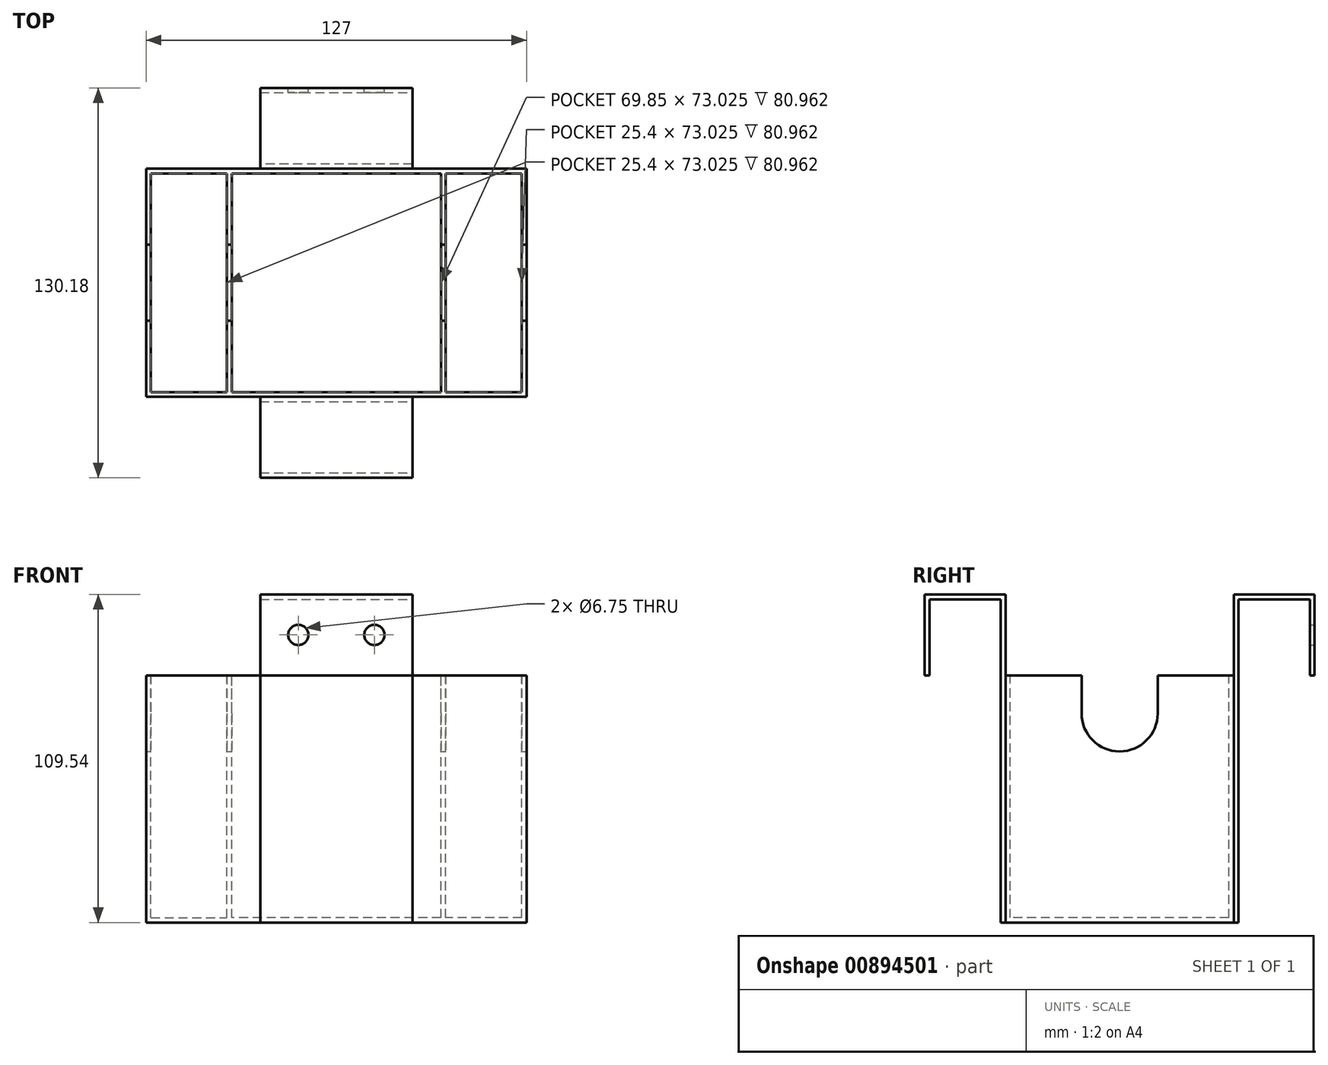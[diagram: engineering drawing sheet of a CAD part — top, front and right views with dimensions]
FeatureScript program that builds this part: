
annotation { "Feature Type Name" : "Feature", "Feature Type Description" : "" }
export const myFeature = defineFeature(function(context is Context, id is Id, definition is map)
    precondition{}
    {
        {
            var Q0;
            Q0=qCreatedBy(makeId("Top.planeOp"),FACE);
            var sketch = newSketch(context, id + "F0", { "sketchPlane" : qUnion([Q0])});
            skLineSegment(sketch, "E0.bottom", {"start": v(63.5, 38.1) * mm, "end": v(-63.5, 38.1) * mm});
            skLineSegment(sketch, "E0.top", {"start": v(63.5, -38.1) * mm, "end": v(-63.5, -38.1) * mm});
            skLineSegment(sketch, "E0.left", {"start": v(63.5, 38.1) * mm, "end": v(63.5, -38.1) * mm});
            skLineSegment(sketch, "E0.right", {"start": v(-63.5, 38.1) * mm, "end": v(-63.5, -38.1) * mm});
            skPoint(sketch, "E1.end.orphan", {"position": v(0, 38.1) * mm});
            skPoint(sketch, "E2.end.orphan", {"position": v(63.5, 0) * mm});
            skSolve(sketch);
        }
        {
            var Q0;
            Q0=makeQuery(id+"F0.imprint","IMPRINT",FACE,{"disambiguationData":[TD([[makeQuery(id+"F0.imprint","IMPRINT",EDGE,{"derivedFrom":sQuery(id+"F0.wireOp",EDGE,"E0.bottom")}),1.0]])]});
            extrude(context, id + "F1", {"entities" : qUnion([Q0]), "depth" : 82.55 * mm, "offsetDistance" : 25.4 * mm});
        }
        {
            var Q0;
            Q0=makeQuery(id+"F1.opExtrude","CAP_FACE",FACE,{"disambiguationData":[OSD([sQuery(id+"F0.wireOp",EDGE,"E0.bottom"),sQuery(id+"F0.wireOp",EDGE,"E0.top"),sQuery(id+"F0.wireOp",EDGE,"E0.left"),sQuery(id+"F0.wireOp",EDGE,"E0.right")])],"isStart":false});
            var sketch = newSketch(context, id + "F2", { "sketchPlane" : qUnion([Q0])});
            skSolve(sketch);
        }
        {
            var Q0;
            Q0=makeQuery(id+"F2.imprint","IMPRINT",FACE,{"disambiguationData":[TD([[makeQuery(id+"F2.imprint","IMPRINT",EDGE,{"derivedFrom":makeQuery(id+"F1.opExtrude","CAP_EDGE",EDGE,{"disambiguationData":[OSD([sQuery(id+"F0.wireOp",EDGE,"E0.bottom")])],"isStart":false})}),1.0]])]});
            var sketch = newSketch(context, id + "F3", { "sketchPlane" : qUnion([Q0])});
            skLineSegment(sketch, "E3", {"start": v(-61.91, 0) * mm, "end": v(-61.91, -36.51) * mm});
            skLineSegment(sketch, "E4.top", {"start": v(-61.91, 36.51) * mm, "end": v(-36.51, 36.51) * mm});
            skLineSegment(sketch, "E4.left", {"start": v(-61.91, -36.51) * mm, "end": v(-61.91, 36.51) * mm});
            skLineSegment(sketch, "E4.right", {"start": v(61.91, -36.51) * mm, "end": v(61.91, 36.51) * mm});
            skLineSegment(sketch, "E5", {"start": v(-61.91, -36.51) * mm, "end": v(-36.51, -36.51) * mm});
            skLineSegment(sketch, "E6", {"start": v(-36.51, -36.51) * mm, "end": v(-36.51, 36.51) * mm});
            skLineSegment(sketch, "E7", {"start": v(-34.93, 36.51) * mm, "end": v(-34.93, -36.51) * mm});
            skLineSegment(sketch, "E8", {"start": v(61.91, -36.51) * mm, "end": v(36.51, -36.51) * mm});
            skLineSegment(sketch, "E9", {"start": v(36.51, -36.51) * mm, "end": v(36.51, 36.51) * mm});
            skLineSegment(sketch, "E10", {"start": v(34.92, 36.51) * mm, "end": v(34.92, -36.51) * mm});
            skLineSegment(sketch, "E11", {"start": v(34.92, -36.51) * mm, "end": v(-34.93, -36.51) * mm});
            skLineSegment(sketch, "E12.trimOffspring", {"start": v(-34.93, 36.51) * mm, "end": v(34.92, 36.51) * mm});
            skLineSegment(sketch, "E13.trimOffspring", {"start": v(36.51, 36.51) * mm, "end": v(61.91, 36.51) * mm});
            skSolve(sketch);
        }
        {
            var Q0;
            Q0 = qSketchRegion(id + "F3", true);
            extrude(context, id + "F4", {"entities" : qUnion([Q0]), "operationType" : NewBodyOperationType.REMOVE, "oppositeDirection" : true, "depth" : 80.96 * mm, "offsetDistance" : 25.4 * mm});
        }
        {
            var Q0;
            Q0=makeQuery(id+"F1.opExtrude","SWEPT_FACE",FACE,{"disambiguationData":[OSD([sQuery(id+"F0.wireOp",EDGE,"E0.left")])]});
            var sketch = newSketch(context, id + "F5", { "sketchPlane" : qUnion([Q0])});
            skLineSegment(sketch, "E14.0", {"start": v(12.7, 82.55) * mm, "end": v(-12.7, 82.55) * mm});
            skLineSegment(sketch, "E15", {"start": v(0, 82.55) * mm, "end": v(-12.7, 82.55) * mm});
            skLineSegment(sketch, "E16", {"start": v(-12.7, 82.55) * mm, "end": v(-12.7, 69.85) * mm});
            skLineSegment(sketch, "E17", {"start": v(12.7, 69.85) * mm, "end": v(12.7, 82.55) * mm});
            skLineSegment(sketch, "E18", {"start": v(12.7, 82.55) * mm, "end": v(0, 82.55) * mm});
            skPoint(sketch, "E19.0.end.orphan", {"position": v(38.1, 0) * mm});
            skPoint(sketch, "E20.orphan", {"position": v(38.1, 82.55) * mm});
            skPoint(sketch, "E21.0.end.orphan", {"position": v(-38.1, 0) * mm});
            skPoint(sketch, "E21.0.start.orphan", {"position": v(-38.1, 82.55) * mm});
            skLineSegment(sketch, "E22", {"start": v(0, 57.15) * mm, "end": v(0, 69.85) * mm});
            skArc(sketch, "E23", {"start": v(-12.7, 69.85) * mm, "mid": v(0, 57.15) * mm, "end": v(12.7, 69.85) * mm});
            skSolve(sketch);
        }
        {
            var Q0;
            Q0 = qSketchRegion(id + "F5", true);
            extrude(context, id + "F6", {"entities" : qUnion([Q0]), "operationType" : NewBodyOperationType.REMOVE, "endBound" : BoundingType.THROUGH_ALL, "oppositeDirection" : true, "depth" : 25.4 * mm, "offsetDistance" : 25.4 * mm});
        }
        {
            var Q0;
            Q0=makeQuery(id+"F1.opExtrude","SWEPT_FACE",FACE,{"disambiguationData":[OSD([sQuery(id+"F0.wireOp",EDGE,"E0.top")])]});
            var sketch = newSketch(context, id + "F7", { "sketchPlane" : qUnion([Q0])});
            skLineSegment(sketch, "E24", {"start": v(0, 0) * mm, "end": v(12.7, 0) * mm});
            skPoint(sketch, "E25", {"position": v(12.7, 82.55) * mm});
            skLineSegment(sketch, "E26", {"start": v(0, 0) * mm, "end": v(-12.7, 0) * mm});
            skLineSegment(sketch, "E27", {"start": v(-12.7, 107.95) * mm, "end": v(12.7, 107.95) * mm});
            skLineSegment(sketch, "E28", {"start": v(0, 0) * mm, "end": v(25.4, 0) * mm});
            skLineSegment(sketch, "E29", {"start": v(25.4, 0) * mm, "end": v(25.4, 107.95) * mm});
            skLineSegment(sketch, "E30", {"start": v(0, 0) * mm, "end": v(-25.4, 0) * mm});
            skLineSegment(sketch, "E31", {"start": v(-25.4, 0) * mm, "end": v(-25.4, 107.95) * mm});
            skLineSegment(sketch, "E32", {"start": v(-25.4, 107.95) * mm, "end": v(25.4, 107.95) * mm});
            skSolve(sketch);
        }
        {
            var Q0;
            Q0 = qSketchRegion(id + "F7", true);
            extrude(context, id + "F8", {"entities" : qUnion([Q0]), "operationType" : NewBodyOperationType.ADD, "depth" : 1.59 * mm, "offsetDistance" : 25.4 * mm});
        }
        {
            var Q0;
            Q0=makeQuery(id+"F1.opExtrude","SWEPT_FACE",FACE,{"disambiguationData":[OSD([sQuery(id+"F0.wireOp",EDGE,"E0.bottom")])]});
            var sketch = newSketch(context, id + "F9", { "sketchPlane" : qUnion([Q0])});
            skLineSegment(sketch, "E33", {"start": v(0, 0) * mm, "end": v(12.7, 0) * mm});
            skLineSegment(sketch, "E34", {"start": v(12.7, 107.95) * mm, "end": v(-12.7, 107.95) * mm});
            skLineSegment(sketch, "E35", {"start": v(-12.7, 0) * mm, "end": v(0, 0) * mm});
            skLineSegment(sketch, "E36", {"start": v(0, 0) * mm, "end": v(25.4, 0) * mm});
            skLineSegment(sketch, "E37", {"start": v(25.4, 0) * mm, "end": v(25.4, 107.95) * mm});
            skLineSegment(sketch, "E38", {"start": v(25.4, 107.95) * mm, "end": v(-25.4, 107.95) * mm});
            skLineSegment(sketch, "E39", {"start": v(-25.4, 107.95) * mm, "end": v(-25.4, 0) * mm});
            skLineSegment(sketch, "E40", {"start": v(-25.4, 0) * mm, "end": v(-12.7, 0) * mm});
            skSolve(sketch);
        }
        {
            var Q0;
            {var subQ10=sQuery(id+"F9.wireOp",EDGE,"E35");Q0=makeQuery(id+"F9.imprint","IMPRINT",FACE,{"disambiguationData":[TD([[makeQuery(id+"F9.imprint","IMPRINT",EDGE,{"derivedFrom":subQ10}),1.0]])]});}
            var Q1;
            {var subQ0=sQuery(id+"F9.wireOp",EDGE,"E38");var subQ1=sQuery(id+"F9.wireOp",EDGE,"E37");var subQ2=makeQuery(id+"F9.imprint","INTERSECT",VERTEX,{"derivedFrom":[subQ1,subQ0]});Q1=makeQuery(id+"F9.imprint","IMPRINT",FACE,{"disambiguationData":[TD([[makeQuery(id+"F9.imprint","IMPRINT",EDGE,{"disambiguationData":[TD([[subQ2,1.0]])],"derivedFrom":subQ1}),1.0]])]});}
            extrude(context, id + "F10", {"entities" : qUnion([Q0, Q1]), "operationType" : NewBodyOperationType.ADD, "depth" : 1.59 * mm, "offsetDistance" : 25.4 * mm});
        }
        {
            var Q0;
            Q0=makeQuery(id+"F10.opExtrude","SWEPT_FACE",FACE,{"disambiguationData":[OSD([sQuery(id+"F9.wireOp",EDGE,"E38")])]});
            var sketch = newSketch(context, id + "F11", { "sketchPlane" : qUnion([Q0])});
            skLineSegment(sketch, "E41.bottom", {"start": v(25.4, 38.1) * mm, "end": v(-25.4, 38.1) * mm});
            skLineSegment(sketch, "E41.top", {"start": v(25.4, 65.09) * mm, "end": v(-25.4, 65.09) * mm});
            skLineSegment(sketch, "E41.left", {"start": v(25.4, 38.1) * mm, "end": v(25.4, 65.09) * mm});
            skLineSegment(sketch, "E41.right", {"start": v(-25.4, 38.1) * mm, "end": v(-25.4, 65.09) * mm});
            skLineSegment(sketch, "E42.MirrorCS", {"start": v(25.4, -65.09) * mm, "end": v(-25.4, -65.09) * mm});
            skLineSegment(sketch, "E43.MirrorCS", {"start": v(-25.4, -38.1) * mm, "end": v(-25.4, -65.09) * mm});
            skLineSegment(sketch, "E44.MirrorCS", {"start": v(25.4, -38.1) * mm, "end": v(25.4, -65.09) * mm});
            skLineSegment(sketch, "E45.MirrorCS", {"start": v(25.4, -38.1) * mm, "end": v(-25.4, -38.1) * mm});
            skSolve(sketch);
        }
        {
            var Q0;
            Q0=makeQuery(id+"F11.imprint","IMPRINT",FACE,{"disambiguationData":[TD([[makeQuery(id+"F11.imprint","IMPRINT",EDGE,{"derivedFrom":sQuery(id+"F11.wireOp",EDGE,"E42.MirrorCS")}),-1.0]])]});
            var Q1;
            {var subQ0=sQuery(id+"F11.wireOp",EDGE,"E41.bottom");Q1=makeQuery(id+"F11.imprint","IMPRINT",FACE,{"disambiguationData":[TD([[makeQuery(id+"F11.imprint","IMPRINT",EDGE,{"derivedFrom":subQ0}),1.0]])]});}
            var Q2;
            {var subQ0=sQuery(id+"F11.wireOp",EDGE,"E41.top");Q2=makeQuery(id+"F11.imprint","IMPRINT",FACE,{"disambiguationData":[TD([[makeQuery(id+"F11.imprint","IMPRINT",EDGE,{"derivedFrom":subQ0}),1.0]])]});}
            extrude(context, id + "F12", {"entities" : qUnion([Q0, Q1, Q2]), "operationType" : NewBodyOperationType.ADD, "depth" : 1.59 * mm, "offsetDistance" : 25.4 * mm});
        }
        {
            var Q0;
            Q0=makeQuery(id+"F12.opExtrude","CAP_FACE",FACE,{"disambiguationData":[OSD([sQuery(id+"F11.wireOp",EDGE,"E42.MirrorCS"),sQuery(id+"F11.wireOp",EDGE,"E43.MirrorCS"),sQuery(id+"F11.wireOp",EDGE,"E44.MirrorCS"),sQuery(id+"F11.wireOp",EDGE,"E45.MirrorCS")])],"isStart":true});
            var sketch = newSketch(context, id + "F13", { "sketchPlane" : qUnion([Q0])});
            skLineSegment(sketch, "E46.bottom", {"start": v(-25.4, 65.09) * mm, "end": v(25.4, 65.09) * mm});
            skLineSegment(sketch, "E46.top", {"start": v(-25.4, 63.5) * mm, "end": v(25.4, 63.5) * mm});
            skLineSegment(sketch, "E46.left", {"start": v(-25.4, 65.09) * mm, "end": v(-25.4, 63.5) * mm});
            skLineSegment(sketch, "E46.right", {"start": v(25.4, 65.09) * mm, "end": v(25.4, 63.5) * mm});
            skLineSegment(sketch, "E47.MirrorCS", {"start": v(-25.4, -65.09) * mm, "end": v(-25.4, -63.5) * mm});
            skLineSegment(sketch, "E48.MirrorCS", {"start": v(25.4, -65.09) * mm, "end": v(25.4, -63.5) * mm});
            skLineSegment(sketch, "E49.MirrorCS", {"start": v(-25.4, -65.09) * mm, "end": v(25.4, -65.09) * mm});
            skLineSegment(sketch, "E50.MirrorCS", {"start": v(-25.4, -63.5) * mm, "end": v(25.4, -63.5) * mm});
            skSolve(sketch);
        }
        {
            var Q0;
            Q0=makeQuery(id+"F13.imprint","IMPRINT",FACE,{"disambiguationData":[TD([[makeQuery(id+"F13.imprint","IMPRINT",EDGE,{"derivedFrom":sQuery(id+"F13.wireOp",EDGE,"E46.bottom")}),1.0]])]});
            var Q1;
            Q1=makeQuery(id+"F13.imprint","IMPRINT",FACE,{"disambiguationData":[TD([[makeQuery(id+"F13.imprint","IMPRINT",EDGE,{"derivedFrom":sQuery(id+"F13.wireOp",EDGE,"E47.MirrorCS")}),-1.0]])]});
            extrude(context, id + "F14", {"entities" : qUnion([Q0, Q1]), "operationType" : NewBodyOperationType.ADD, "depth" : 25.4 * mm, "offsetDistance" : 25.4 * mm});
        }
        {
            var Q0;
            Q0=makeQuery(id+"F14.boolean.opBoolean","MERGE",FACE,{"derivedFrom":[makeQuery(id+"F12.opExtrude","SWEPT_FACE",FACE,{"disambiguationData":[OSD([sQuery(id+"F11.wireOp",EDGE,"E42.MirrorCS")])]}),makeQuery(id+"F14.opExtrude","SWEPT_FACE",FACE,{"disambiguationData":[OSD([sQuery(id+"F13.wireOp",EDGE,"E46.bottom")])]})]});
            var sketch = newSketch(context, id + "F15", { "sketchPlane" : qUnion([Q0])});
            skLineSegment(sketch, "E51", {"start": v(25.4, 82.55) * mm, "end": v(0, 82.55) * mm});
            skCircle(sketch, "E52", {"center": v(12.7, 96.04) * mm, "radius": 3.37 * mm});
            skCircle(sketch, "E53.MirrorC", {"center": v(-12.7, 96.04) * mm, "radius": 3.37 * mm});
            skSolve(sketch);
        }
        {
            var Q0;
            Q0 = qSketchRegion(id + "F15", true);
            extrude(context, id + "F16", {"entities" : qUnion([Q0]), "operationType" : NewBodyOperationType.REMOVE, "oppositeDirection" : true, "depth" : 1 / 406.4 * mm, "offsetDistance" : 25.4 * mm});
        }
        {
            var Q0;
            Q0=makeQuery(id+"F14.boolean.opBoolean","MERGE",FACE,{"derivedFrom":[makeQuery(id+"F12.opExtrude","SWEPT_FACE",FACE,{"disambiguationData":[OSD([sQuery(id+"F11.wireOp",EDGE,"E41.top")])]}),makeQuery(id+"F14.opExtrude","SWEPT_FACE",FACE,{"disambiguationData":[OSD([sQuery(id+"F13.wireOp",EDGE,"E49.MirrorCS")])]})]});
            var sketch = newSketch(context, id + "F17", { "sketchPlane" : qUnion([Q0])});
            skCircle(sketch, "E54", {"center": v(12.7, 96.04) * mm, "radius": 3.37 * mm});
            skCircle(sketch, "E55.MirrorC", {"center": v(-12.7, 96.04) * mm, "radius": 3.37 * mm});
            skSolve(sketch);
        }
        {
            var Q0;
            Q0 = qSketchRegion(id + "F17", true);
            extrude(context, id + "F18", {"entities" : qUnion([Q0]), "operationType" : NewBodyOperationType.REMOVE, "oppositeDirection" : true, "depth" : 1.59 * mm, "offsetDistance" : 25.4 * mm});
        }
    });
